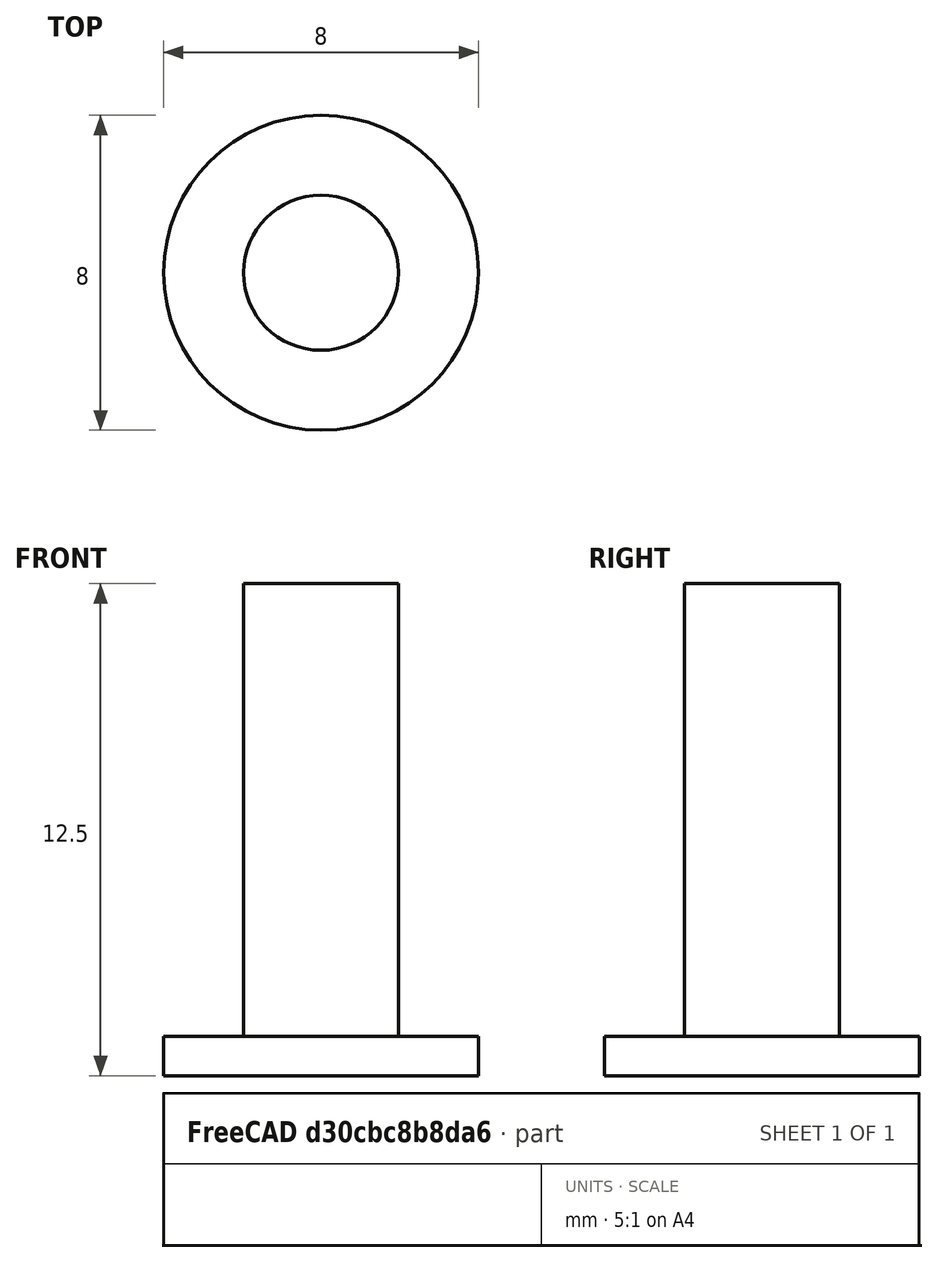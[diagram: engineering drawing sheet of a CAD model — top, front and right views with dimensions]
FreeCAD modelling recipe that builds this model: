
FCSTD DOCUMENT  (FreeCAD 0.18.1R)
Label: pin arm valve techdraw 2
License: All rights reserved
LicenseURL: http://en.wikipedia.org/wiki/All_rights_reserved
objects: TechDraw::DrawViewDimension×7, TechDraw::DrawProjGroupItem×4, Part::Cylinder×2, Part::MultiFuse×1, TechDraw::DrawSVGTemplate×1, TechDraw::DrawProjGroup×1, TechDraw::DrawPage×1
note: 3 computed .brp shape members not serialized (recipe doc carries the construction recipe); baked Part::Feature solids carry a one-line shape summary decoded from their .brp

FEATURE [Part::Cylinder] Cylinder
  Angle = 360
  AttacherType = Attacher::AttachEngine3D
  Height = 1
  Radius = 4
FEATURE [Part::Cylinder] Cylinder001
  Angle = 360
  AttacherType = Attacher::AttachEngine3D
  Height = 11.5
  Placement = pos=(0,0,1) rot=(0,0,1;0rad)
  Radius = 1.97
FEATURE [Part::MultiFuse] Fusion
  Shapes = -> [Cylinder,Cylinder001]
FEATURE [TechDraw::DrawSVGTemplate] Template
  EditableTexts = Designed_by_Name=Designed by Name; Drawing_number=Drawing number; FC-Date=Date; FC-SC=Scale; FC-SH=Sheet; FC-Title=Title; Subtitle=Subtitle; Weight=Weight
  Height = 210
  Orientation = 1
  Width = 297
FEATURE [TechDraw::DrawProjGroupItem] ProjItem  label="Front"
  CoarseView = false
  Direction = (0,-1,0)
  Focus = 100
  HardHidden = false
  IsoCount = 0
  IsoHidden = false
  IsoVisible = false
  LockPosition = true
  Perspective = false
  Rotation = 0
  RotationVector = (1,0,0)
  Scale = 3
  ScaleType = 2
  SeamHidden = false
  SeamVisible = false
  SmoothHidden = false
  SmoothVisible = false
  Source = -> [Fusion]
  Type = 0
  X = 0
  Y = 0
FEATURE [TechDraw::DrawProjGroupItem] ProjItem001  label="Left"
  CoarseView = false
  Direction = (-1,-1e-16,0)
  Focus = 100
  HardHidden = false
  IsoCount = 0
  IsoHidden = false
  IsoVisible = false
  LockPosition = false
  Perspective = false
  Rotation = 0
  RotationVector = (1e-16,-1,0)
  Scale = 3
  ScaleType = 2
  SeamHidden = false
  SeamVisible = false
  SmoothHidden = false
  SmoothVisible = false
  Source = -> [Fusion]
  Type = 1
  X = 55.959
  Y = 0
FEATURE [TechDraw::DrawProjGroupItem] ProjItem002  label="FrontTopLeft"
  CoarseView = false
  Direction = (-1,-1,1)
  Focus = 100
  HardHidden = false
  IsoCount = 0
  IsoHidden = false
  IsoVisible = false
  LockPosition = false
  Perspective = false
  Rotation = 0
  RotationVector = (1,-1,0)
  Scale = 3
  ScaleType = 2
  SeamHidden = false
  SeamVisible = false
  SmoothHidden = false
  SmoothVisible = false
  Source = -> [Fusion]
  Type = 6
  X = 55.959
  Y = -55.959
FEATURE [TechDraw::DrawProjGroupItem] ProjItem003  label="Top"
  CoarseView = false
  Direction = (0,0,1)
  Focus = 100
  HardHidden = false
  IsoCount = 0
  IsoHidden = false
  IsoVisible = false
  LockPosition = false
  Perspective = false
  Rotation = 0
  RotationVector = (1,0,0)
  Scale = 3
  ScaleType = 2
  SeamHidden = false
  SeamVisible = false
  SmoothHidden = false
  SmoothVisible = false
  Source = -> [Fusion]
  Type = 4
  X = 0
  Y = -55.959
FEATURE [TechDraw::DrawProjGroup] ProjGroup
  Anchor = -> ProjItem
  AutoDistribute = true
  LockPosition = false
  ProjectionType = 1
  Rotation = 0
  Scale = 3
  ScaleType = 2
  Source = -> [Fusion]
  Views = -> [ProjItem,ProjItem001,ProjItem002,ProjItem003]
  X = 109.562
  Y = 145.107
  spacingX = 15
  spacingY = 15
FEATURE [TechDraw::DrawViewDimension] Dimension
  Arbitrary = false
  FormatSpec = %.2f
  LockPosition = false
  MeasureType = 1
  OverTolerance = 0
  References2D = -> [ProjItem]
  Rotation = 0
  ScaleType = 0
  Type = 2
  UnderTolerance = 0
  X = -35.5032
  Y = 4.61507
FEATURE [TechDraw::DrawViewDimension] Dimension001
  Arbitrary = false
  FormatSpec = %.2f
  LockPosition = false
  MeasureType = 1
  OverTolerance = 0
  References2D = -> [ProjItem]
  Rotation = 0
  ScaleType = 0
  Type = 2
  UnderTolerance = 0
  X = -23.9994
  Y = -15.3644
FEATURE [TechDraw::DrawViewDimension] Dimension002
  Arbitrary = false
  FormatSpec = %.2f
  LockPosition = false
  MeasureType = 1
  OverTolerance = 0
  References2D = -> [ProjItem]
  Rotation = 0
  ScaleType = 0
  Type = 1
  UnderTolerance = 0
  X = -0.822818
  Y = -32.9436
FEATURE [TechDraw::DrawViewDimension] Dimension003
  Arbitrary = false
  FormatSpec = %.2f
  LockPosition = false
  MeasureType = 1
  OverTolerance = 0
  References2D = -> [ProjItem]
  Rotation = 0
  ScaleType = 0
  Type = 1
  UnderTolerance = 0
  X = -1.02852
  Y = -32.6178
FEATURE [TechDraw::DrawViewDimension] Dimension004
  Arbitrary = false
  FormatSpec = %.2f
  LockPosition = false
  MeasureType = 1
  OverTolerance = 0
  References2D = -> [ProjItem]
  Rotation = 0
  ScaleType = 0
  Type = 1
  UnderTolerance = 0
  X = 1.02852
  Y = 30.0637
FEATURE [TechDraw::DrawViewDimension] Dimension005
  Arbitrary = false
  FormatSpec = ⌀%.2f
  LockPosition = false
  MeasureType = 1
  OverTolerance = 0
  References2D = -> [ProjItem003]
  Rotation = 0
  ScaleType = 0
  Type = 5
  UnderTolerance = 0
  X = 1.23423
  Y = -34.3526
FEATURE [TechDraw::DrawViewDimension] Dimension006
  Arbitrary = false
  FormatSpec = ⌀%.2f
  LockPosition = false
  MeasureType = 1
  OverTolerance = 0
  References2D = -> [ProjItem003]
  Rotation = 0
  ScaleType = 0
  Type = 5
  UnderTolerance = 0
  X = 1.64564
  Y = -46.9006
FEATURE [TechDraw::DrawPage] Page
  KeepUpdated = true
  ProjectionType = 0
  Template = -> Template
  Views = -> [ProjGroup,Dimension,Dimension001,Dimension002,Dimension003,Dimension004,Dimension005,Dimension006]
